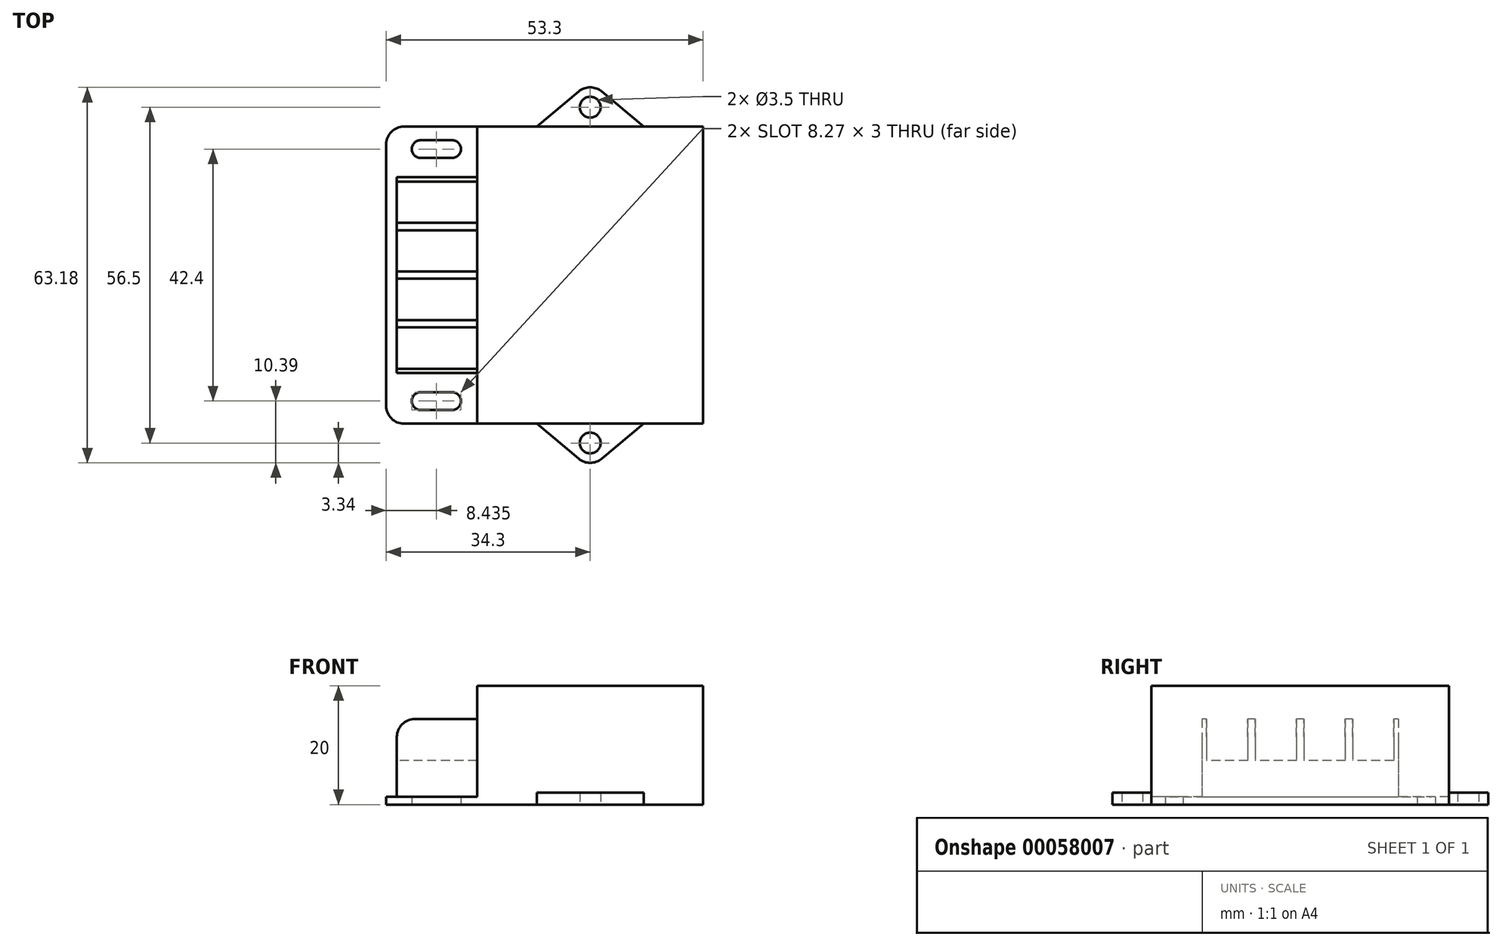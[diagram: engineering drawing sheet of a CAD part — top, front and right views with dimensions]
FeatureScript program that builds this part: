
annotation { "Feature Type Name" : "Feature", "Feature Type Description" : "" }
export const myFeature = defineFeature(function(context is Context, id is Id, definition is map)
    precondition{}
    {
        {
            var Q0;
            Q0=qCreatedBy(makeId("Top.planeOp"),FACE);
            var sketch = newSketch(context, id + "F0", { "sketchPlane" : qUnion([Q0])});
            skLineSegment(sketch, "E0.bottom", {"start": v(3, 0) * mm, "end": v(53.3, 0) * mm});
            skLineSegment(sketch, "E0.top", {"start": v(3, 50) * mm, "end": v(53.3, 50) * mm});
            skLineSegment(sketch, "E0.left", {"start": v(0, 3) * mm, "end": v(0, 47) * mm});
            skLineSegment(sketch, "E0.right", {"start": v(53.3, 0) * mm, "end": v(53.3, 50) * mm});
            skLineSegment(sketch, "E1", {"start": v(15.3, 50) * mm, "end": v(15.3, 0) * mm});
            skLineSegment(sketch, "E2", {"start": v(25.3, 0) * mm, "end": v(32.38, -5.9) * mm});
            skLineSegment(sketch, "E3", {"start": v(36.22, -5.9) * mm, "end": v(43.3, 0) * mm});
            skLineSegment(sketch, "E4", {"start": v(34.3, -7.5) * mm, "end": v(34.3, 0) * mm, "construction": true});
            skLineSegment(sketch, "E5", {"start": v(15.3, 40.83) * mm, "end": v(53.3, 40.83) * mm, "construction": true});
            skLineSegment(sketch, "E6", {"start": v(34.3, 0) * mm, "end": v(53.3, 0) * mm, "construction": true});
            skLineSegment(sketch, "E7", {"start": v(34.3, -7.5) * mm, "end": v(53.3, -7.5) * mm, "construction": true});
            skLineSegment(sketch, "E8", {"start": v(53.3, -7.5) * mm, "end": v(53.3, 0) * mm, "construction": true});
            skLineSegment(sketch, "E9", {"start": v(25.3, 0) * mm, "end": v(25.3, 7.78) * mm, "construction": true});
            skLineSegment(sketch, "E10", {"start": v(25.3, 7.78) * mm, "end": v(43.3, 7.78) * mm, "construction": true});
            skLineSegment(sketch, "E11", {"start": v(43.3, 7.78) * mm, "end": v(43.3, 0) * mm, "construction": true});
            skLineSegment(sketch, "E12", {"start": v(34.3, 0) * mm, "end": v(34.3, -1.5) * mm, "construction": true});
            skLineSegment(sketch, "E13", {"start": v(34.3, -1.5) * mm, "end": v(34.3, -3.25) * mm, "construction": true});
            skCircle(sketch, "E14", {"center": v(34.3, -3.25) * mm, "radius": 1.75 * mm});
            skPoint(sketch, "E15.visualSharp", {"position": v(34.3, -7.5) * mm});
            skArc(sketch, "E15.filletArc", {"start": v(32.38, -5.9) * mm, "mid": v(34.3, -6.6) * mm, "end": v(36.22, -5.9) * mm});
            skPoint(sketch, "E16.visualSharp", {"position": v(0, 50) * mm});
            skArc(sketch, "E16.filletArc", {"start": v(3, 50) * mm, "mid": v(0.88, 49.12) * mm, "end": v(0, 47) * mm});
            skPoint(sketch, "E17.visualSharp", {"position": v(0, 0) * mm});
            skArc(sketch, "E17.filletArc", {"start": v(0, 3) * mm, "mid": v(0.88, 0.88) * mm, "end": v(3, 0) * mm});
            skLineSegment(sketch, "E18", {"start": v(0, 25) * mm, "end": v(53.3, 25) * mm, "construction": true});
            skLineSegment(sketch, "E19.MirrorCS", {"start": v(36.22, 55.9) * mm, "end": v(43.3, 50) * mm});
            skArc(sketch, "E20.MirrorCS", {"start": v(32.38, 55.9) * mm, "mid": v(34.3, 56.6) * mm, "end": v(36.22, 55.9) * mm});
            skLineSegment(sketch, "E21.MirrorCS", {"start": v(25.3, 50) * mm, "end": v(32.38, 55.9) * mm});
            skLineSegment(sketch, "E22", {"start": v(0, 3.8) * mm, "end": v(5.8, 3.8) * mm, "construction": true});
            skLineSegment(sketch, "E23", {"start": v(5.8, 3.8) * mm, "end": v(11.07, 3.8) * mm, "construction": true});
            skLineSegment(sketch, "E24", {"start": v(11.07, 3.8) * mm, "end": v(11.07, 0) * mm, "construction": true});
            skArc(sketch, "E25.0.startCap", {"start": v(5.8, 2.3) * mm, "mid": v(4.3, 3.8) * mm, "end": v(5.8, 5.3) * mm});
            skArc(sketch, "E25.0.endCap", {"start": v(11.07, 5.3) * mm, "mid": v(12.57, 3.8) * mm, "end": v(11.07, 2.3) * mm});
            skLineSegment(sketch, "E25.0.left", {"start": v(5.8, 5.3) * mm, "end": v(11.07, 5.3) * mm});
            skLineSegment(sketch, "E25.0.right", {"start": v(5.8, 2.3) * mm, "end": v(11.07, 2.3) * mm});
            skLineSegment(sketch, "E26.MirrorCS", {"start": v(5.8, 44.7) * mm, "end": v(11.07, 44.7) * mm});
            skArc(sketch, "E27.MirrorCS", {"start": v(11.07, 44.7) * mm, "mid": v(12.57, 46.2) * mm, "end": v(11.07, 47.7) * mm});
            skLineSegment(sketch, "E28.MirrorCS", {"start": v(5.8, 47.7) * mm, "end": v(11.07, 47.7) * mm});
            skArc(sketch, "E29.MirrorCS", {"start": v(5.8, 47.7) * mm, "mid": v(4.3, 46.2) * mm, "end": v(5.8, 44.7) * mm});
            skCircle(sketch, "E30.MirrorC", {"center": v(34.3, 53.25) * mm, "radius": 1.75 * mm});
            skSolve(sketch);
        }
        {
            var Q0;
            {var subQ3=sQuery(id+"F0.wireOp",EDGE,"E0.right");Q0=makeQuery(id+"F0.imprint","IMPRINT",FACE,{"disambiguationData":[TD([[makeQuery(id+"F0.imprint","IMPRINT",EDGE,{"derivedFrom":subQ3}),1.0]])]});}
            extrude(context, id + "F1", {"entities" : qUnion([Q0]), "depth" : 20 * mm});
        }
        {
            var Q0;
            {var subQ1=sQuery(id+"F0.wireOp",EDGE,"E2");Q0=makeQuery(id+"F0.imprint","IMPRINT",FACE,{"disambiguationData":[TD([[makeQuery(id+"F0.imprint","IMPRINT",EDGE,{"derivedFrom":subQ1}),1.0]])]});}
            var Q1;
            {var subQ0=sQuery(id+"F0.wireOp",EDGE,"E19.MirrorCS");Q1=makeQuery(id+"F0.imprint","IMPRINT",FACE,{"disambiguationData":[TD([[makeQuery(id+"F0.imprint","IMPRINT",EDGE,{"derivedFrom":subQ0}),-1.0]])]});}
            extrude(context, id + "F2", {"entities" : qUnion([Q0, Q1]), "operationType" : NewBodyOperationType.ADD, "depth" : 2 * mm});
        }
        {
            var Q0;
            Q0=makeQuery(id+"F0.imprint","IMPRINT",FACE,{"disambiguationData":[TD([[makeQuery(id+"F0.imprint","IMPRINT",EDGE,{"derivedFrom":sQuery(id+"F0.wireOp",EDGE,"E0.left")}),-1.0]])]});
            extrude(context, id + "F3", {"entities" : qUnion([Q0]), "operationType" : NewBodyOperationType.ADD, "depth" : 1.3 * mm});
        }
        {
            var Q0;
            Q0=makeQuery(id+"F3.opExtrude","CAP_FACE",FACE,{"disambiguationData":[OSD([sQuery(id+"F0.wireOp",EDGE,"E0.bottom"),sQuery(id+"F0.wireOp",EDGE,"E0.top"),sQuery(id+"F0.wireOp",EDGE,"E0.left"),sQuery(id+"F0.wireOp",EDGE,"E1"),sQuery(id+"F0.wireOp",EDGE,"E16.filletArc"),sQuery(id+"F0.wireOp",EDGE,"E17.filletArc"),sQuery(id+"F0.wireOp",EDGE,"E25.0.startCap"),sQuery(id+"F0.wireOp",EDGE,"E25.0.endCap"),sQuery(id+"F0.wireOp",EDGE,"E25.0.left"),sQuery(id+"F0.wireOp",EDGE,"E25.0.right"),sQuery(id+"F0.wireOp",EDGE,"E26.MirrorCS"),sQuery(id+"F0.wireOp",EDGE,"E27.MirrorCS"),sQuery(id+"F0.wireOp",EDGE,"E28.MirrorCS"),sQuery(id+"F0.wireOp",EDGE,"E29.MirrorCS")])],"isStart":false});
            var sketch = newSketch(context, id + "F4", { "sketchPlane" : qUnion([Q0])});
            skLineSegment(sketch, "E31.0", {"start": v(15.3, 41.5) * mm, "end": v(15.3, 8.5) * mm});
            skLineSegment(sketch, "E32.0", {"start": v(15.3, 25) * mm, "end": v(53.3, 25) * mm});
            skLineSegment(sketch, "E33.top", {"start": v(15.3, 41.5) * mm, "end": v(1.8, 41.5) * mm});
            skLineSegment(sketch, "E33.left", {"start": v(15.3, 25) * mm, "end": v(15.3, 41.5) * mm});
            skLineSegment(sketch, "E33.right", {"start": v(1.8, 25) * mm, "end": v(1.8, 41.5) * mm});
            skLineSegment(sketch, "E34.top", {"start": v(15.3, 8.5) * mm, "end": v(1.8, 8.5) * mm});
            skLineSegment(sketch, "E34.left", {"start": v(15.3, 25) * mm, "end": v(15.3, 8.5) * mm});
            skLineSegment(sketch, "E34.right", {"start": v(1.8, 25) * mm, "end": v(1.8, 8.5) * mm});
            skPoint(sketch, "E35.orphan", {"position": v(0, 25) * mm});
            skPoint(sketch, "E36.orphan", {"position": v(15.3, 50) * mm});
            skPoint(sketch, "E37.orphan", {"position": v(15.3, 0) * mm});
            skLineSegment(sketch, "E38", {"start": v(1.8, 40.75) * mm, "end": v(15.3, 40.75) * mm});
            skLineSegment(sketch, "E39", {"start": v(1.8, 9.25) * mm, "end": v(15.3, 9.25) * mm});
            skLineSegment(sketch, "E40", {"start": v(8.55, 8.5) * mm, "end": v(8.55, 9.25) * mm, "construction": true});
            skLineSegment(sketch, "E41", {"start": v(8.55, 40.75) * mm, "end": v(8.55, 41.5) * mm, "construction": true});
            skLineSegment(sketch, "E42", {"start": v(1.8, 33.81) * mm, "end": v(15.3, 33.81) * mm});
            skLineSegment(sketch, "E43", {"start": v(1.8, 32.56) * mm, "end": v(15.3, 32.56) * mm});
            skLineSegment(sketch, "E44", {"start": v(1.8, 25.63) * mm, "end": v(15.3, 25.63) * mm});
            skLineSegment(sketch, "E45", {"start": v(8.55, 32.56) * mm, "end": v(8.55, 33.81) * mm, "construction": true});
            skLineSegment(sketch, "E46", {"start": v(8.55, 32.56) * mm, "end": v(8.55, 25.63) * mm, "construction": true});
            skLineSegment(sketch, "E47", {"start": v(15.3, 25.63) * mm, "end": v(15.3, 24.38) * mm, "construction": true});
            skPoint(sketch, "E48", {"position": v(15.3, 25) * mm});
            skLineSegment(sketch, "E49", {"start": v(8.55, 40.75) * mm, "end": v(8.55, 33.81) * mm, "construction": true});
            skLineSegment(sketch, "E50.MirrorCS", {"start": v(1.8, 17.44) * mm, "end": v(15.3, 17.44) * mm});
            skLineSegment(sketch, "E51.MirrorCS", {"start": v(1.8, 16.19) * mm, "end": v(15.3, 16.19) * mm});
            skLineSegment(sketch, "E52.MirrorCS", {"start": v(1.8, 24.38) * mm, "end": v(15.3, 24.38) * mm});
            skSolve(sketch);
        }
        {
            var Q0;
            {var subQ0=sQuery(id+"F4.wireOp",EDGE,"E38");Q0=makeQuery(id+"F4.imprint","IMPRINT",FACE,{"disambiguationData":[TD([[makeQuery(id+"F4.imprint","IMPRINT",EDGE,{"derivedFrom":subQ0}),-1.0]])]});}
            var Q1;
            {var subQ0=sQuery(id+"F4.wireOp",EDGE,"E42");Q1=makeQuery(id+"F4.imprint","IMPRINT",FACE,{"disambiguationData":[TD([[makeQuery(id+"F4.imprint","IMPRINT",EDGE,{"derivedFrom":subQ0}),-1.0]])]});}
            var Q2;
            {var subQ0=sQuery(id+"F4.wireOp",EDGE,"E43");Q2=makeQuery(id+"F4.imprint","IMPRINT",FACE,{"disambiguationData":[TD([[makeQuery(id+"F4.imprint","IMPRINT",EDGE,{"derivedFrom":subQ0}),-1.0]])]});}
            var Q3;
            {var subQ4=sQuery(id+"F4.wireOp",EDGE,"E44");Q3=makeQuery(id+"F4.imprint","IMPRINT",FACE,{"disambiguationData":[TD([[makeQuery(id+"F4.imprint","IMPRINT",EDGE,{"derivedFrom":subQ4}),-1.0]])]});}
            var Q4;
            {var subQ0=sQuery(id+"F4.wireOp",EDGE,"E50.MirrorCS");Q4=makeQuery(id+"F4.imprint","IMPRINT",FACE,{"disambiguationData":[TD([[makeQuery(id+"F4.imprint","IMPRINT",EDGE,{"derivedFrom":subQ0}),1.0]])]});}
            var Q5;
            {var subQ0=sQuery(id+"F4.wireOp",EDGE,"E50.MirrorCS");Q5=makeQuery(id+"F4.imprint","IMPRINT",FACE,{"disambiguationData":[TD([[makeQuery(id+"F4.imprint","IMPRINT",EDGE,{"derivedFrom":subQ0}),-1.0]])]});}
            var Q6;
            {var subQ0=sQuery(id+"F4.wireOp",EDGE,"E39");Q6=makeQuery(id+"F4.imprint","IMPRINT",FACE,{"disambiguationData":[TD([[makeQuery(id+"F4.imprint","IMPRINT",EDGE,{"derivedFrom":subQ0}),1.0]])]});}
            var Q7;
            {var subQ0=sQuery(id+"F4.wireOp",EDGE,"E34.top");Q7=makeQuery(id+"F4.imprint","IMPRINT",FACE,{"disambiguationData":[TD([[makeQuery(id+"F4.imprint","IMPRINT",EDGE,{"derivedFrom":subQ0}),-1.0]])]});}
            var Q8;
            {var subQ0=sQuery(id+"F4.wireOp",EDGE,"E33.top");Q8=makeQuery(id+"F4.imprint","IMPRINT",FACE,{"disambiguationData":[TD([[makeQuery(id+"F4.imprint","IMPRINT",EDGE,{"derivedFrom":subQ0}),1.0]])]});}
            extrude(context, id + "F5", {"entities" : qUnion([Q0, Q1, Q2, Q3, Q4, Q5, Q6, Q7, Q8]), "operationType" : NewBodyOperationType.ADD, "depth" : 6.1 * mm});
        }
        {
            var Q0;
            {var subQ0=sQuery(id+"F4.wireOp",EDGE,"E33.top");Q0=makeQuery(id+"F4.imprint","IMPRINT",FACE,{"disambiguationData":[TD([[makeQuery(id+"F4.imprint","IMPRINT",EDGE,{"derivedFrom":subQ0}),1.0]])]});}
            var Q1;
            {var subQ0=sQuery(id+"F4.wireOp",EDGE,"E34.top");Q1=makeQuery(id+"F4.imprint","IMPRINT",FACE,{"disambiguationData":[TD([[makeQuery(id+"F4.imprint","IMPRINT",EDGE,{"derivedFrom":subQ0}),-1.0]])]});}
            var Q2;
            {var subQ0=sQuery(id+"F4.wireOp",EDGE,"E42");Q2=makeQuery(id+"F4.imprint","IMPRINT",FACE,{"disambiguationData":[TD([[makeQuery(id+"F4.imprint","IMPRINT",EDGE,{"derivedFrom":subQ0}),-1.0]])]});}
            var Q3;
            {var subQ4=sQuery(id+"F4.wireOp",EDGE,"E44");Q3=makeQuery(id+"F4.imprint","IMPRINT",FACE,{"disambiguationData":[TD([[makeQuery(id+"F4.imprint","IMPRINT",EDGE,{"derivedFrom":subQ4}),-1.0]])]});}
            var Q4;
            {var subQ0=sQuery(id+"F4.wireOp",EDGE,"E50.MirrorCS");Q4=makeQuery(id+"F4.imprint","IMPRINT",FACE,{"disambiguationData":[TD([[makeQuery(id+"F4.imprint","IMPRINT",EDGE,{"derivedFrom":subQ0}),-1.0]])]});}
            extrude(context, id + "F6", {"entities" : qUnion([Q0, Q1, Q2, Q3, Q4]), "operationType" : NewBodyOperationType.ADD, "depth" : 13.1 * mm});
        }
        {
            var Q0;
            {var subQ0=sQuery(id+"F4.wireOp",EDGE,"E33.right");Q0=makeQuery(id+"F6.opExtrude","CAP_EDGE",EDGE,{"disambiguationData":[OSD([subQ0]),TDD([makeQuery(id+"F4.imprint","IMPRINT",EDGE,{"disambiguationData":[TD([[makeQuery(id+"F4.imprint","INTERSECT",VERTEX,{"derivedFrom":[sQuery(id+"F4.wireOp",EDGE,"E33.top"),subQ0]}),1.0]])],"derivedFrom":subQ0})])],"isStart":false});}
            var Q1;
            {var subQ0=sQuery(id+"F4.wireOp",EDGE,"E33.right");Q1=makeQuery(id+"F6.opExtrude","CAP_EDGE",EDGE,{"disambiguationData":[OSD([subQ0]),TDD([makeQuery(id+"F4.imprint","IMPRINT",EDGE,{"disambiguationData":[TD([[makeQuery(id+"F4.imprint","INTERSECT",VERTEX,{"derivedFrom":[subQ0,sQuery(id+"F4.wireOp",EDGE,"E42")]}),1.0]])],"derivedFrom":subQ0})])],"isStart":false});}
            var Q2;
            Q2=makeQuery(id+"F6.opExtrude","CAP_EDGE",EDGE,{"disambiguationData":[OSD([sQuery(id+"F4.wireOp",EDGE,"E33.right"),sQuery(id+"F4.wireOp",EDGE,"E34.right")])],"isStart":false});
            var Q3;
            {var subQ0=sQuery(id+"F4.wireOp",EDGE,"E34.right");Q3=makeQuery(id+"F6.opExtrude","CAP_EDGE",EDGE,{"disambiguationData":[OSD([subQ0]),TDD([makeQuery(id+"F4.imprint","IMPRINT",EDGE,{"disambiguationData":[TD([[makeQuery(id+"F4.imprint","INTERSECT",VERTEX,{"derivedFrom":[subQ0,sQuery(id+"F4.wireOp",EDGE,"E50.MirrorCS")]}),-1.0]])],"derivedFrom":subQ0})])],"isStart":false});}
            var Q4;
            {var subQ0=sQuery(id+"F4.wireOp",EDGE,"E34.right");Q4=makeQuery(id+"F6.opExtrude","CAP_EDGE",EDGE,{"disambiguationData":[OSD([subQ0]),TDD([makeQuery(id+"F4.imprint","IMPRINT",EDGE,{"disambiguationData":[TD([[makeQuery(id+"F4.imprint","INTERSECT",VERTEX,{"derivedFrom":[sQuery(id+"F4.wireOp",EDGE,"E34.top"),subQ0]}),1.0]])],"derivedFrom":subQ0})])],"isStart":false});}
            fillet(context, id + "F7", {"entities" : qUnion([Q0, Q1, Q2, Q3, Q4]), "radius" : 3 * mm, "tangentPropagation" : true, "allowEdgeOverflow" : false});
        }
    });
